# Revit family: HERZ-Thermostatkopf MINI Turbo M28x1.5 9200 13
name_source: partatom
category: Rohrzubehör
units: mm (PartAtom-declared; Revit-internal decimal feet)

## family parameters
Arbeitsebenenbasiert = Nein
Beim Laden mit Abzugskörper schneiden = Nein
Bemaßung runder Anschluss = Durchmesser verwenden
Gemeinsam genutzt = Nein
Immer vertikal = Nein
OmniClass-Nummer = 23.65.55.14
OmniClass-Titel = Valves for Liquid Services
Teiletyp = Normal

## types (1)
- HERZ-Thermostatkopf MINI Turbo M28x1.5 9200 13
    Anwendungen = Zur Montage auf Ventilen, die für thermostatischen Betrieb eingerichtet sind.Artikelnummern, Dimensionen und Lieferform der HERZ Ventile sind den jeweiligen Produktnormblättern zu entnehmen.
    Bestellnummer = 1920013
    Frostsicherung = Heizkörperthermostat  mit  Flüssigkeitsfühler  (Hydrosensor)  mit  automatischer  Frostsicherung  und  Be-grenzung und Blockierung des Sollwertbereiches.
    Frostsicherung bei = 6 °C
    Funktionsweise = Der HERZ-Thermostat dient als Fühl- und Regelelement. Durch die Volumsänderung der Flüssigkeitsfüllung im HERZ-Hydrosensor wird die Schubspindel des Ventils bewegt.
    Hersteller = HERZ Armaturen Ges.m.b.H.
    Nullstellung = Heizkörperthermostat mit Flüssigkeitsfühler (Hydrosensor) mit Stellung „0“, Frostsicherung einstellbar, mit Begrenzung und Blockierung des Sollwertbereiches.
    S01 = 73 mm  [stored 0.239501 ft]
    S02 = 60 mm  [stored 0.19685 ft]
    Sollwertbereich = 0-30°C
    Sollwertbereich Frostsicherung = 6-30°C
    Thermostatkopf = Kunststoff, weiß
    URL = www.herz-armaturen.at
    Vorgabe-Ansicht = 0 mm  [stored 0 ft]

note: [stored X ft] marks values corroborated as IEEE doubles in the binary element streams (Revit-internal decimal feet)
